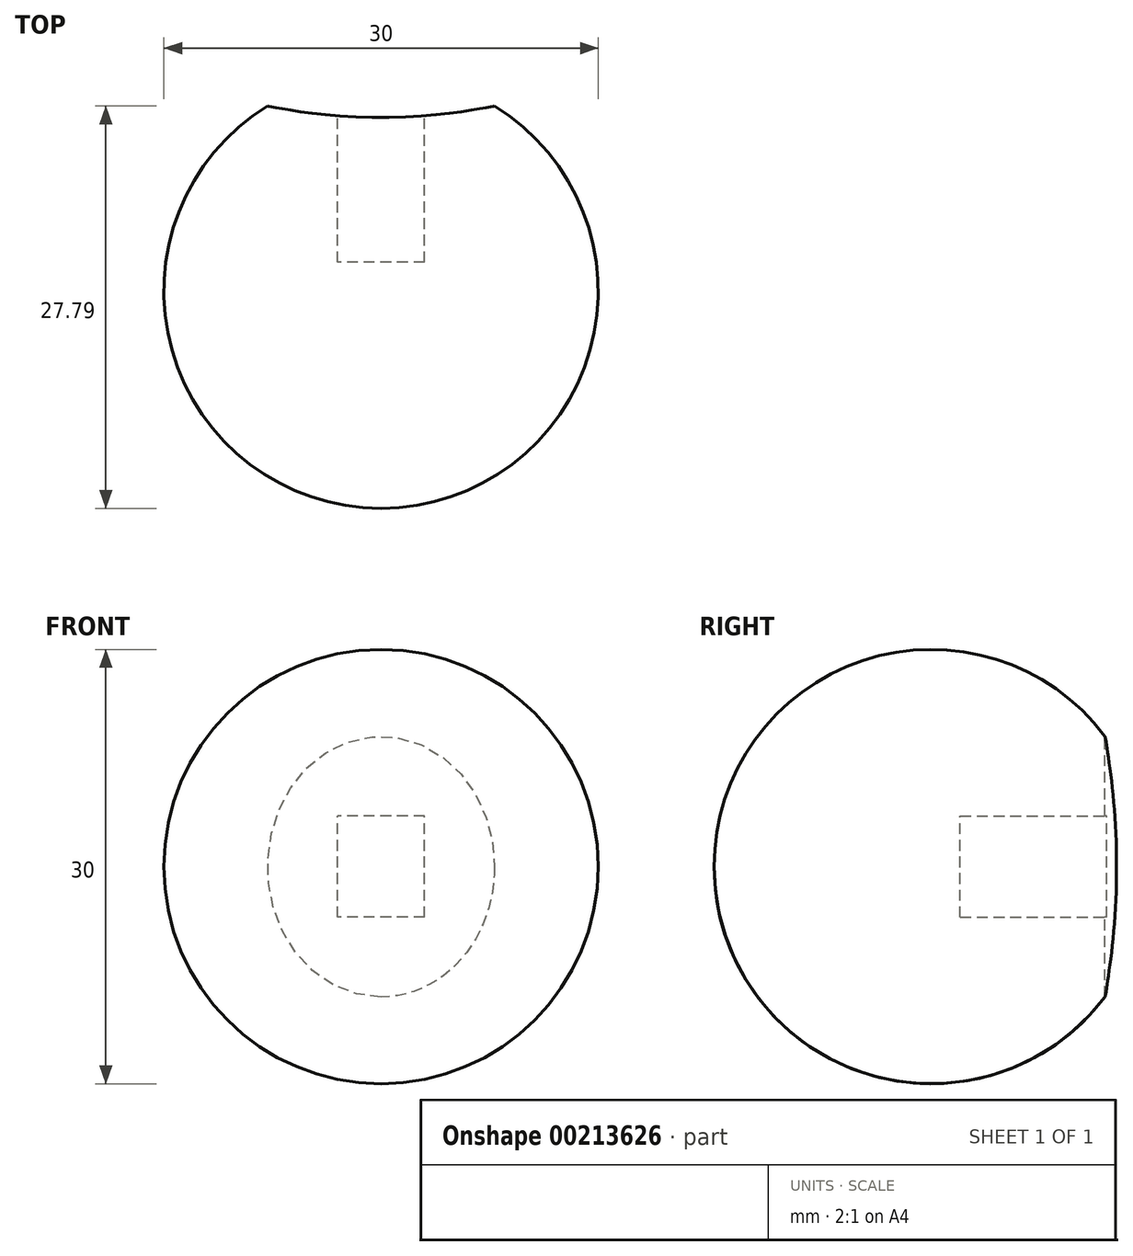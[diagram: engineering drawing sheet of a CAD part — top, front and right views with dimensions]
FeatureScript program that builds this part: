
annotation { "Feature Type Name" : "Feature", "Feature Type Description" : "" }
export const myFeature = defineFeature(function(context is Context, id is Id, definition is map)
    precondition{}
    {
        {
            var Q0;
            Q0=qCreatedBy(makeId("Right.planeOp"),FACE);
            var sketch = newSketch(context, id + "F0", { "sketchPlane" : qUnion([Q0])});
            skLineSegment(sketch, "E0", {"start": v(0, 0) * mm, "end": v(-30, 0) * mm});
            skArc(sketch, "E1", {"start": v(0, 0) * mm, "mid": v(-15, 15) * mm, "end": v(-30, 0) * mm});
            skSolve(sketch);
        }
        {
            var Q0;
            Q0 = qSketchRegion(id + "F0", true);
            var Q1;
            Q1=sQuery(id+"F0.wireOp",EDGE,"E0");
            revolve(context, id + "F1", {"entities" : qUnion([Q0]), "axis" : qUnion([Q1]), "revolveType" : RevolveType.FULL});
        }
        {
            var Q0;
            Q0=qCreatedBy(makeId("Top.planeOp"),FACE);
            cPlane(context, id + "F2", {"entities" : qUnion([Q0]), "cplaneType" : CPlaneType.OFFSET, "offset" : 15 * mm, "width" : 150 * mm, "height" : 150 * mm});
        }
        {
            var Q0;
            Q0=qCreatedBy(id+"F2.planeOp",FACE);
            var sketch = newSketch(context, id + "F3", { "sketchPlane" : qUnion([Q0])});
            skLineSegment(sketch, "E2", {"start": v(0, 0) * mm, "end": v(0, -16.03) * mm, "construction": true});
            skLineSegment(sketch, "E3", {"start": v(0, 0) * mm, "end": v(-15, 0) * mm});
            skLineSegment(sketch, "E4", {"start": v(0, 0) * mm, "end": v(15, 0) * mm});
            skArc(sketch, "E5", {"start": v(-15, 0) * mm, "mid": v(0, -3) * mm, "end": v(15, 0) * mm});
            skSolve(sketch);
        }
        {
            var Q0;
            Q0 = qSketchRegion(id + "F3", true);
            extrude(context, id + "F4", {"entities" : qUnion([Q0]), "operationType" : NewBodyOperationType.REMOVE, "endBound" : BoundingType.THROUGH_ALL, "oppositeDirection" : true, "depth" : 25 * mm});
        }
        {
            var Q0;
            Q0=qCreatedBy(makeId("Front.planeOp"),FACE);
            var sketch = newSketch(context, id + "F5", { "sketchPlane" : qUnion([Q0])});
            skLineSegment(sketch, "E6.bottom", {"start": v(3, -3.5) * mm, "end": v(-3, -3.5) * mm});
            skLineSegment(sketch, "E6.top", {"start": v(3, 3.5) * mm, "end": v(-3, 3.5) * mm});
            skLineSegment(sketch, "E6.left", {"start": v(3, -3.5) * mm, "end": v(3, 3.5) * mm});
            skLineSegment(sketch, "E6.right", {"start": v(-3, -3.5) * mm, "end": v(-3, 3.5) * mm});
            skPoint(sketch, "E6.middle", {"position": v(0, 0) * mm});
            skSolve(sketch);
        }
        {
            var Q0;
            Q0 = qSketchRegion(id + "F5", true);
            extrude(context, id + "F6", {"entities" : qUnion([Q0]), "operationType" : NewBodyOperationType.REMOVE, "depth" : 13 * mm});
        }
    });
